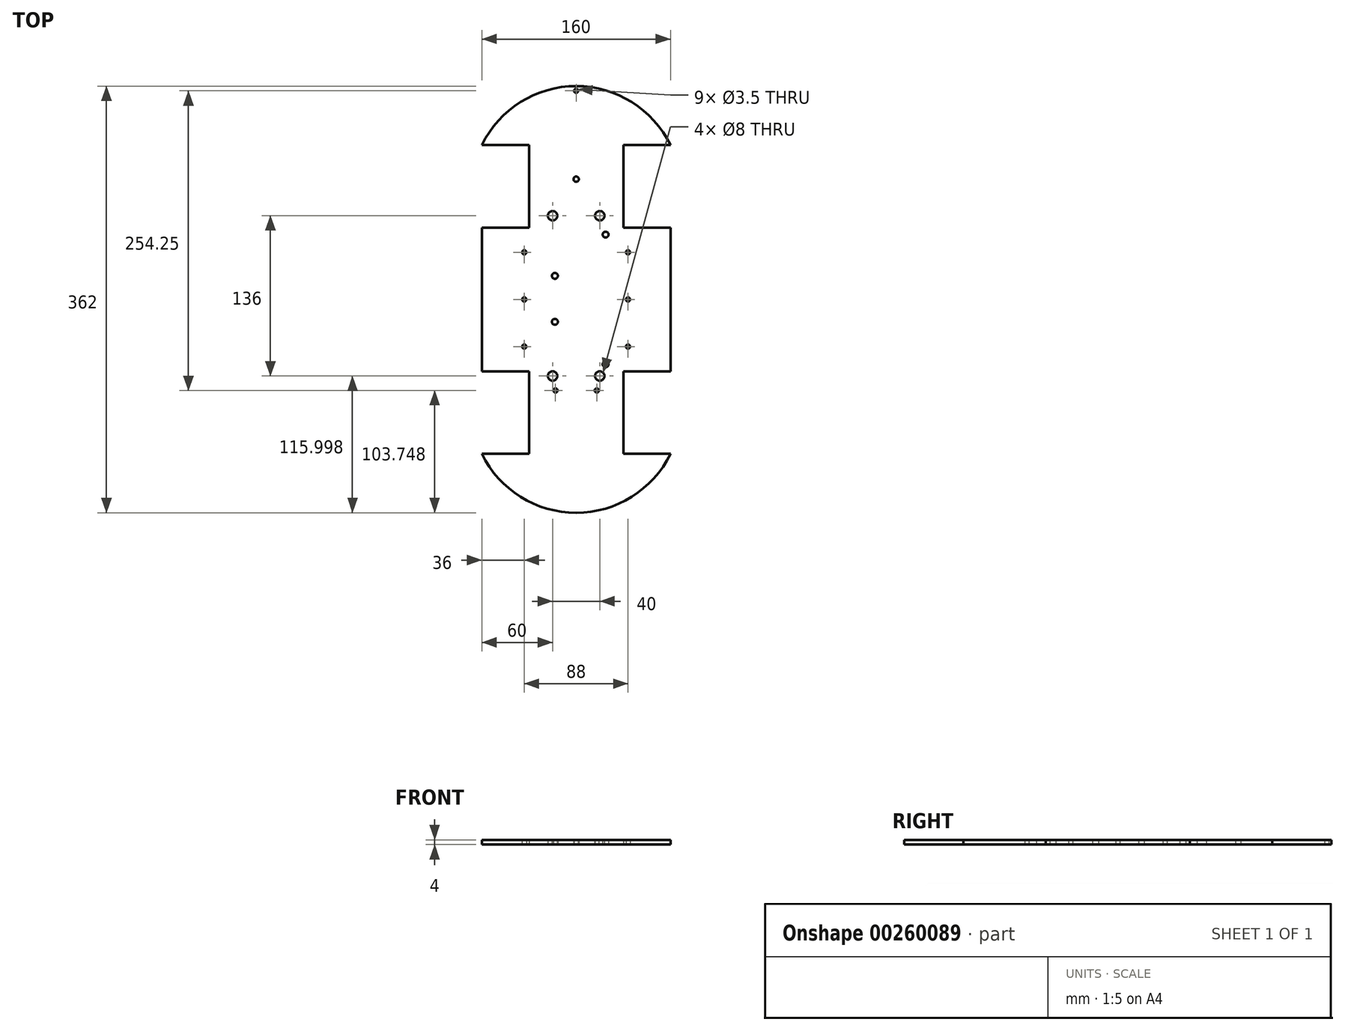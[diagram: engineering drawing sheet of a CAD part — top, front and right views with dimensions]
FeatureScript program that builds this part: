
annotation { "Feature Type Name" : "Feature", "Feature Type Description" : "" }
export const myFeature = defineFeature(function(context is Context, id is Id, definition is map)
    precondition{}
    {
        {
            var Q0;
            Q0=qCreatedBy(makeId("Top.planeOp"),FACE);
            var sketch = newSketch(context, id + "F0", { "sketchPlane" : qUnion([Q0])});
            skLineSegment(sketch, "E0.bottom", {"start": v(-80, 169.49) * mm, "end": v(-40, 169.49) * mm});
            skLineSegment(sketch, "E0.top", {"start": v(-80, -92.51) * mm, "end": v(-40, -92.51) * mm});
            skLineSegment(sketch, "E0.left", {"start": v(-80, 99.49) * mm, "end": v(-80, -22.51) * mm});
            skLineSegment(sketch, "E1.top", {"start": v(-80, 99.49) * mm, "end": v(-40, 99.49) * mm});
            skLineSegment(sketch, "E1.right", {"start": v(-40, 169.49) * mm, "end": v(-40, 99.49) * mm});
            skLineSegment(sketch, "E2.bottom", {"start": v(-80, -22.51) * mm, "end": v(-40, -22.51) * mm});
            skLineSegment(sketch, "E2.right", {"start": v(-40, -22.51) * mm, "end": v(-40, -92.51) * mm});
            skLineSegment(sketch, "E3.MirrorCS", {"start": v(80, 169.49) * mm, "end": v(40, 169.49) * mm});
            skLineSegment(sketch, "E4.MirrorCS", {"start": v(40, 169.49) * mm, "end": v(40, 99.49) * mm});
            skLineSegment(sketch, "E5.MirrorCS", {"start": v(80, 99.49) * mm, "end": v(40, 99.49) * mm});
            skLineSegment(sketch, "E6.MirrorCS", {"start": v(80, 99.49) * mm, "end": v(80, -22.51) * mm});
            skLineSegment(sketch, "E7.MirrorCS", {"start": v(80, -22.51) * mm, "end": v(40, -22.51) * mm});
            skLineSegment(sketch, "E8.MirrorCS", {"start": v(40, -22.51) * mm, "end": v(40, -92.51) * mm});
            skArc(sketch, "E9", {"start": v(80, 169.49) * mm, "mid": v(0, 219.49) * mm, "end": v(-80, 169.49) * mm});
            skLineSegment(sketch, "E10.MirrorCS", {"start": v(80, -92.51) * mm, "end": v(40, -92.51) * mm});
            skArc(sketch, "E11", {"start": v(-80, -92.51) * mm, "mid": v(0, -142.51) * mm, "end": v(80, -92.51) * mm});
            skPoint(sketch, "E12.positionSnap0", {"position": v(-40, 134.49) * mm});
            skPoint(sketch, "E13.orphan", {"position": v(0, 169.49) * mm});
            skCircle(sketch, "E14", {"center": v(0, 215.49) * mm, "radius": 1.75 * mm});
            skCircle(sketch, "E15", {"center": v(-44, 78.49) * mm, "radius": 1.75 * mm});
            skCircle(sketch, "E16", {"center": v(-44, 38.49) * mm, "radius": 1.75 * mm});
            skCircle(sketch, "E17", {"center": v(-44, -1.51) * mm, "radius": 1.75 * mm});
            skCircle(sketch, "E18.MirrorC", {"center": v(44, 78.49) * mm, "radius": 1.75 * mm});
            skCircle(sketch, "E19.MirrorC", {"center": v(44, 38.49) * mm, "radius": 1.75 * mm});
            skCircle(sketch, "E20.MirrorC", {"center": v(44, -1.51) * mm, "radius": 1.75 * mm});
            skCircle(sketch, "E21", {"center": v(-18, 58.49) * mm, "radius": 2.5 * mm});
            skCircle(sketch, "E22", {"center": v(-18, 19.49) * mm, "radius": 2.5 * mm});
            skCircle(sketch, "E23", {"center": v(25, 93.49) * mm, "radius": 2.5 * mm});
            skCircle(sketch, "E24", {"center": v(25, -16.51) * mm, "radius": 2.5 * mm});
            skCircle(sketch, "E25", {"center": v(-20, -26.51) * mm, "radius": 4 * mm});
            skCircle(sketch, "E26.MirrorC", {"center": v(20, -26.51) * mm, "radius": 4 * mm});
            skCircle(sketch, "E27", {"center": v(-17.5, -38.76) * mm, "radius": 1.75 * mm});
            skCircle(sketch, "E28.MirrorC", {"center": v(17.5, -38.76) * mm, "radius": 1.75 * mm});
            skCircle(sketch, "E29", {"center": v(-20, 109.49) * mm, "radius": 4 * mm});
            skCircle(sketch, "E30.MirrorC", {"center": v(20, 109.49) * mm, "radius": 4 * mm});
            skCircle(sketch, "E31", {"center": v(0, 140.49) * mm, "radius": 2.25 * mm});
            skSolve(sketch);
        }
        {
            var Q0;
            Q0 = qSketchRegion(id + "F0", true);
            extrude(context, id + "F1", {"entities" : qUnion([Q0]), "depth" : 4 * mm});
        }
    });
